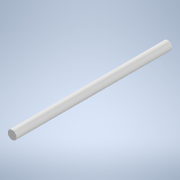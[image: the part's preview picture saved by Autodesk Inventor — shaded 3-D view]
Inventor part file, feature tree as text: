
AUTODESK INVENTOR PART (.ipt)
format: ipt  version: 2020.2 (Build 242310000, 310)  size: 91,136 bytes
history: native  units: in
note: dims shown in document units (in); Inventor stores cm internally (conversion verified against a paired STEP export)
features: extrude x1, sketch x1
ambient origin geometry x8: Origin, YZ Plane, XZ Plane, XY Plane, X Axis, Y Axis, Z Axis, Center Point
bodies: Solid1 (feature_tree)
feature tree (2):
  extrude  "Extrusion1"  Depth=3.5433in TaperAngle=0.0deg
  sketch  "Sketch1"  dims[d0=0.1969in d1=3.5433in d2=0.0in]
